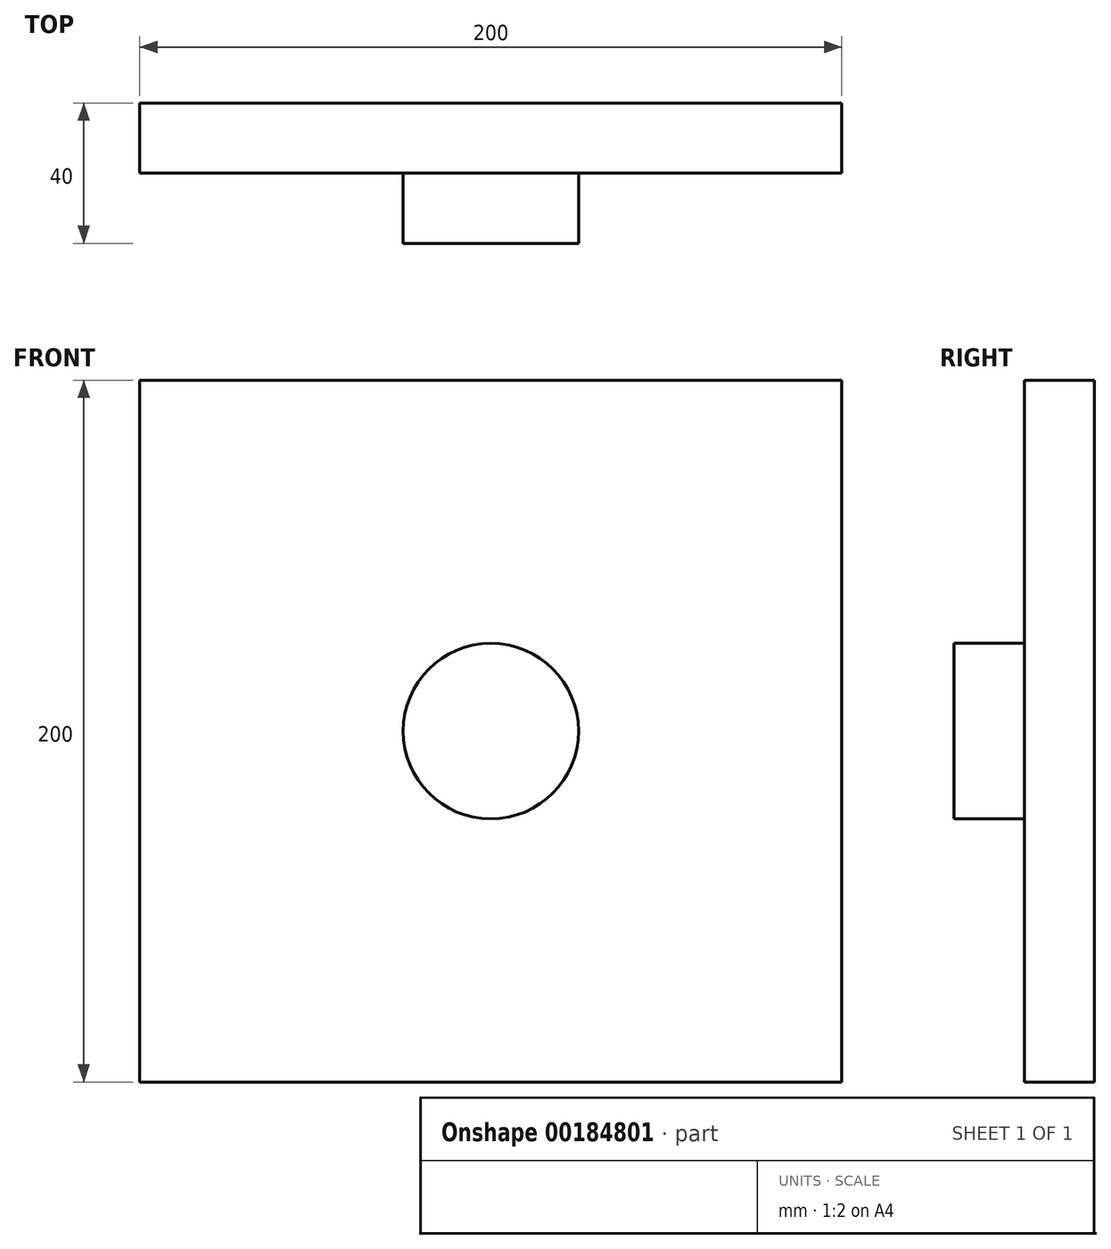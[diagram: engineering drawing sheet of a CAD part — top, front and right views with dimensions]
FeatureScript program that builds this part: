
annotation { "Feature Type Name" : "Feature", "Feature Type Description" : "" }
export const myFeature = defineFeature(function(context is Context, id is Id, definition is map)
    precondition{}
    {
        {
            var Q0;
            Q0=qCreatedBy(makeId("Front.planeOp"),FACE);
            var sketch = newSketch(context, id + "F0", { "sketchPlane" : qUnion([Q0])});
            skLineSegment(sketch, "E0.bottom", {"start": v(0, 0) * mm, "end": v(200, 0) * mm});
            skLineSegment(sketch, "E0.top", {"start": v(0, 200) * mm, "end": v(200, 200) * mm});
            skLineSegment(sketch, "E0.left", {"start": v(0, 0) * mm, "end": v(0, 200) * mm});
            skLineSegment(sketch, "E0.right", {"start": v(200, 0) * mm, "end": v(200, 200) * mm});
            skLineSegment(sketch, "E1", {"start": v(0, 200) * mm, "end": v(200, 0) * mm, "construction": true});
            skLineSegment(sketch, "E2", {"start": v(200, 200) * mm, "end": v(0, 0) * mm, "construction": true});
            skSolve(sketch);
        }
        {
            var Q0;
            Q0=makeQuery(id+"F0.imprint","IMPRINT",FACE,{"disambiguationData":[TD([[makeQuery(id+"F0.imprint","IMPRINT",EDGE,{"derivedFrom":sQuery(id+"F0.wireOp",EDGE,"E0.bottom")}),1.0]])]});
            extrude(context, id + "F1", {"entities" : qUnion([Q0]), "depth" : 20 * mm});
        }
        {
            var Q0;
            Q0=makeQuery(id+"F1.opExtrude","CAP_FACE",FACE,{"disambiguationData":[OSD([sQuery(id+"F0.wireOp",EDGE,"E0.bottom"),sQuery(id+"F0.wireOp",EDGE,"E0.top"),sQuery(id+"F0.wireOp",EDGE,"E0.left"),sQuery(id+"F0.wireOp",EDGE,"E0.right")])],"isStart":false});
            var sketch = newSketch(context, id + "F2", { "sketchPlane" : qUnion([Q0])});
            skLineSegment(sketch, "E3", {"start": v(0, 200) * mm, "end": v(200, 0) * mm, "construction": true});
            skLineSegment(sketch, "E4", {"start": v(0, 0) * mm, "end": v(200, 200) * mm, "construction": true});
            skCircle(sketch, "E5", {"center": v(100, 100) * mm, "radius": 25 * mm});
            skSolve(sketch);
        }
        {
            var Q0;
            Q0 = qSketchRegion(id + "F2", true);
            extrude(context, id + "F3", {"entities" : qUnion([Q0]), "operationType" : NewBodyOperationType.ADD, "depth" : 20 * mm});
        }
    });
